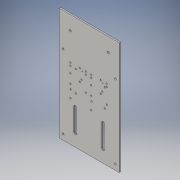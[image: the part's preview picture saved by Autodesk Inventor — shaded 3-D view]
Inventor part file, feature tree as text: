
AUTODESK INVENTOR PART (.ipt)
format: ipt  version: 2016 (Build 200138000, 138)  size: 316,928 bytes
history: native  units: in
note: dims shown in document units (in); Inventor stores cm internally (conversion verified against a paired STEP export)
features: hole x10, other x7, sketch x4, extrude x2
ambient origin geometry x8: Origin, YZ Plane, XZ Plane, XY Plane, X Axis, Y Axis, Z Axis, Center Point
bodies: Solid1 (feature_tree)
feature tree (23):
  extrude  "Extrusion1"  Depth=10.135in
  hole  "Hole1"  [1 undecoded]
  extrude  "Extrusion2"  Depth=3.0in
  hole  "Hole2"  [1 undecoded]
  other  "battery_buzzer"
  other  "grizzly_bear"
  other  "Smartsensor"
  other  "SmartsensorPowered"
  other  "teamflag"
  other  "cape"
  other  "Board Area"
  hole  "Hole3"  [1 undecoded]
  hole  "Hole5"  [1 undecoded]
  hole  "Hole6"  [1 undecoded]
  hole  "Hole7"  [1 undecoded]
  hole  "Hole9"  [1 undecoded]
  hole  "Hole10"  [1 undecoded]
  hole  "Hole11"  [1 undecoded]
  hole  "Hole12"  [1 undecoded]
  sketch  "Sketch1"  dims[d0=5.4in d1=10.135in]
  sketch  "Sketch2"  dims[d2=0.125in d3=0.0in d4=0.35in]
  sketch  "Sketch4"  dims[d5=3.0in d6=3.0in]
  sketch  "Sketch5"  dims[d7=0.35in d8=0.165in d9=0.5in d10=0.35in d11=0.35in d12=0.5in d13=0.165in d14=0.165in d15=0.75in d16=0.375in d17=0.25in d18=0.5635in d19=1.0in d20=0.8108in d21=0.165in d22=0.165in d23=0.27in d24=0.27in d25=1.315in d26=2.0in d27=1.315in d28=1.135in d29=1.135in d30=1.135in d31=1.135in d32=2.0in d33=2.0in d34=2.0in d35=0.125in d36=0.0in d37=1.25in d38=3.412in d39=1.25in d40=0.994in d41=0.176in d42=0.75in d43=0.375in d44=0.25in d45=0.5635in d46=1.0in d47=0.8108in d48=0.7in d49=3.5in d50=3.0in d51=0.7in d52=1.3in d54=0.13in d55=0.13in d57=0.15in d58=0.15in d59=0.15in d60=0.825in d62=1.0in d74=1.3in d75=0.13in d76=0.13in d77=0.15in d78=0.15in d79=0.15in d80=0.825in d81=1.0in d83=0.13in d85=3.0in d86=1.625in d89=0.11in d90=0.125in d91=0.11in d92=1.515in d97=2.88in d98=0.125in d99=2.35in d100=1.1in d101=0.13in d102=0.13in d103=0.13in d104=0.13in d105=0.125in d106=0.15in d107=0.125in d108=0.15in d109=0.125in d110=0.125in d111=0.125in d112=1.2in d128=1.6in d129=1.6in d140=1.4in d141=1.4in d142=1.4in d143=0.1in d144=0.1in d145=1.6in d146=1.6in d147=1.4in d148=1.4in d149=1.4in d150=0.1in d151=0.1in d152=0.125in d153=2.837in d154=2.1496in d155=1.9in d156=0.0in d157=0.125in d158=0.125in d159=1.65in d160=0.0in d161=0.25in d162=0.112in d163=4.0in d164=3.5in d165=0.7in d166=0.13in d168=3.0in d169=1.625in d172=0.11in d173=0.125in d174=0.11in d175=1.515in d180=2.88in d181=0.125in d182=0.25in d186=1.0in d187=3.75in d188=3.75in d189=1.0in d190=1.0in d191=3.75in d192=2.875in d193=2.35in d194=1.1in d195=0.13in d196=0.13in d197=0.13in d198=0.13in d199=0.125in d200=0.15in d201=0.125in d202=0.15in d203=0.125in d204=0.125in d205=0.125in d206=1.2in d207=2.875in d209=1.0in d210=4.0in d211=2.875in d212=4.0in d213=0.13in d214=0.75in d215=0.375in d216=0.25in d217=0.5635in d218=1.0in d219=0.8108in d227=0.13in d228=0.75in d229=0.375in d230=0.25in d231=0.5635in d232=1.0in d233=0.8108in d234=0.13in d235=0.75in d236=0.375in d237=0.25in d238=0.5635in d239=1.0in d240=0.8108in d241=0.13in d242=0.75in d243=0.375in d244=0.25in d245=0.5635in d246=1.0in d247=0.8108in d255=0.079in d256=0.75in d257=0.375in d258=0.25in d259=0.5635in d260=1.0in d261=0.8108in d262=0.079in d263=0.75in d264=0.375in d265=0.25in d266=0.5635in d267=1.0in d268=0.8108in d269=1.5in d270=1.75in d271=0.13in d272=0.75in d273=0.375in d274=0.25in d275=0.5635in d276=1.0in d277=0.8108in d278=0.13in d279=0.75in d280=0.375in d281=0.25in d282=0.5635in d283=1.0in d284=0.8108in d220=1.0in d221=1.0in]
note: 10 required parameter values undecoded (feature->parameter linkage not recoverable at this tier; creation-order binding heuristic only, values carry confidence <= 0.55)
